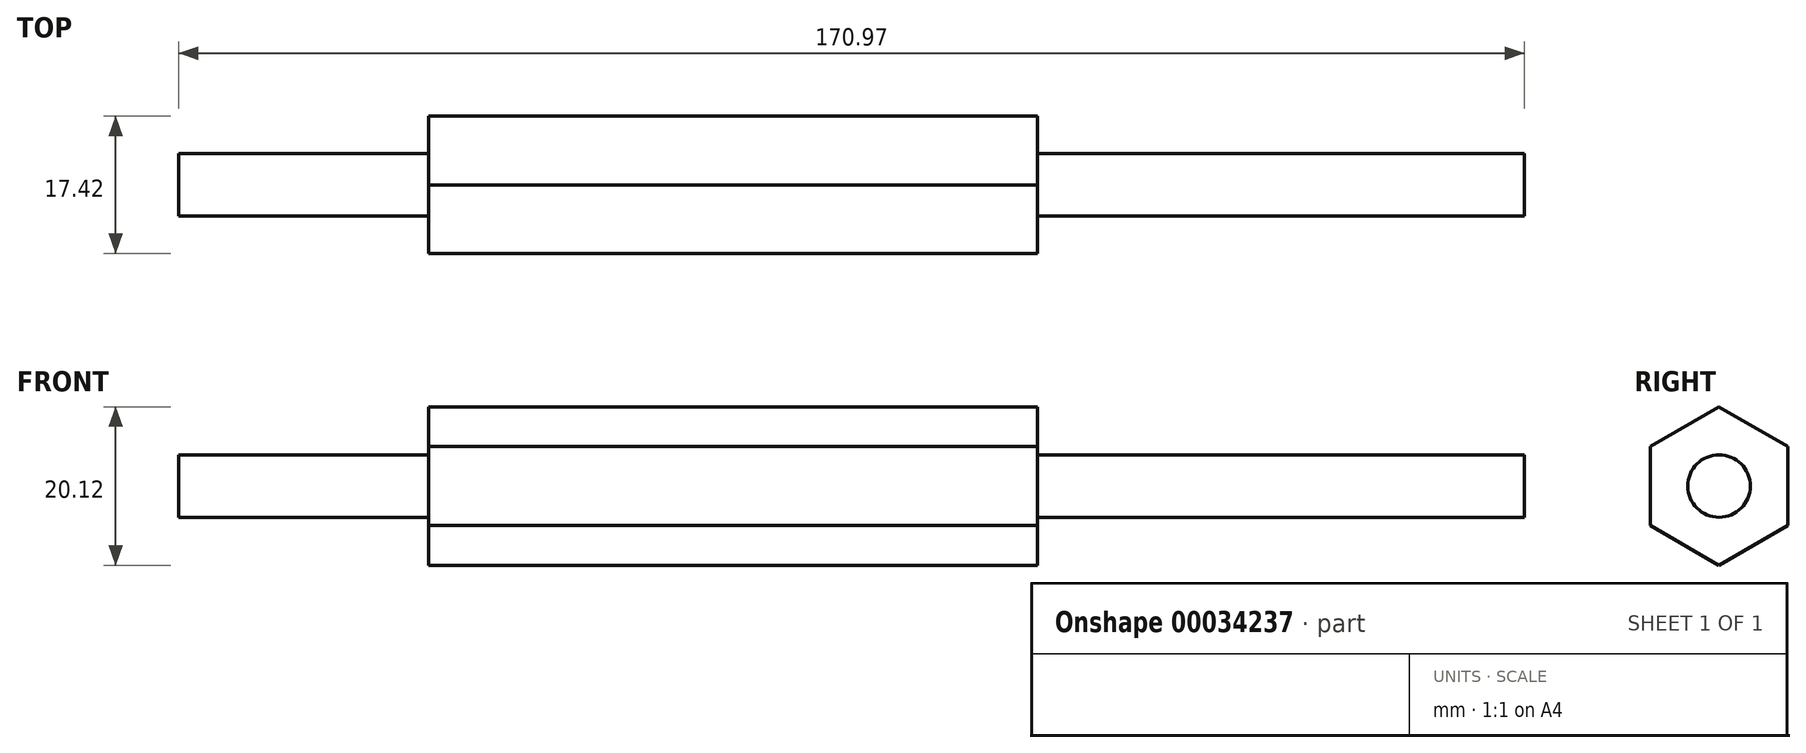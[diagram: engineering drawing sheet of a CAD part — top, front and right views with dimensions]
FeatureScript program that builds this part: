
annotation { "Feature Type Name" : "Feature", "Feature Type Description" : "" }
export const myFeature = defineFeature(function(context is Context, id is Id, definition is map)
    precondition{}
    {
        {
            var Q0;
            Q0=qCreatedBy(makeId("Right.planeOp"),FACE);
            var sketch = newSketch(context, id + "F0", { "sketchPlane" : qUnion([Q0])});
            skCircle(sketch, "E0.cCircle", {"center": v(0, 0) * mm, "radius": 8.71 * mm, "construction": true});
            skLineSegment(sketch, "E0.0", {"start": v(8.71, 5.03) * mm, "end": v(8.71, -5.03) * mm});
            skLineSegment(sketch, "E0.1", {"start": v(8.71, -5.03) * mm, "end": v(0, -10.06) * mm});
            skLineSegment(sketch, "E0.2", {"start": v(0, -10.06) * mm, "end": v(-8.71, -5.03) * mm});
            skLineSegment(sketch, "E0.3", {"start": v(-8.71, -5.03) * mm, "end": v(-8.71, 5.03) * mm});
            skLineSegment(sketch, "E0.4", {"start": v(-8.71, 5.03) * mm, "end": v(0, 10.06) * mm});
            skLineSegment(sketch, "E0.5", {"start": v(0, 10.06) * mm, "end": v(8.71, 5.03) * mm});
            skPoint(sketch, "E0.0.midPoint", {"position": v(8.71, 0) * mm});
            skSolve(sketch);
        }
        {
            var Q0;
            Q0 = qSketchRegion(id + "F0", true);
            extrude(context, id + "F1", {"entities" : qUnion([Q0]), "oppositeDirection" : true, "depth" : 77.32 * mm});
        }
        {
            var Q0;
            Q0=makeQuery(id+"F1.opExtrude","CAP_FACE",FACE,{"disambiguationData":[OSD([sQuery(id+"F0.wireOp",EDGE,"E0.0"),sQuery(id+"F0.wireOp",EDGE,"E0.1"),sQuery(id+"F0.wireOp",EDGE,"E0.2"),sQuery(id+"F0.wireOp",EDGE,"E0.3"),sQuery(id+"F0.wireOp",EDGE,"E0.4"),sQuery(id+"F0.wireOp",EDGE,"E0.5")])],"isStart":false});
            var sketch = newSketch(context, id + "F2", { "sketchPlane" : qUnion([Q0])});
            skCircle(sketch, "E1", {"center": v(0, 0) * mm, "radius": 3.96 * mm});
            skSolve(sketch);
        }
        {
            var Q0;
            Q0 = qSketchRegion(id + "F2", true);
            extrude(context, id + "F3", {"entities" : qUnion([Q0]), "operationType" : NewBodyOperationType.ADD, "depth" : 31.75 * mm});
        }
        {
            var Q0;
            Q0=makeQuery(id+"F1.opExtrude","CAP_FACE",FACE,{"disambiguationData":[OSD([sQuery(id+"F0.wireOp",EDGE,"E0.0"),sQuery(id+"F0.wireOp",EDGE,"E0.1"),sQuery(id+"F0.wireOp",EDGE,"E0.2"),sQuery(id+"F0.wireOp",EDGE,"E0.3"),sQuery(id+"F0.wireOp",EDGE,"E0.4"),sQuery(id+"F0.wireOp",EDGE,"E0.5")])],"isStart":true});
            var sketch = newSketch(context, id + "F4", { "sketchPlane" : qUnion([Q0])});
            skCircle(sketch, "E2", {"center": v(0, 0) * mm, "radius": 3.97 * mm});
            skSolve(sketch);
        }
        {
            var Q0;
            Q0 = qSketchRegion(id + "F4", true);
            extrude(context, id + "F5", {"entities" : qUnion([Q0]), "operationType" : NewBodyOperationType.ADD, "depth" : 61.9 * mm});
        }
    });
